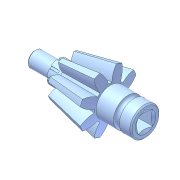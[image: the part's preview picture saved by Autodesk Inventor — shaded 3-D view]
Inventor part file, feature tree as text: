
AUTODESK INVENTOR PART (.ipt)
format: ipt  version: unknown  size: 373,248 bytes
history: native  units: in
note: dims shown in document units (in); Inventor stores cm internally (conversion verified against a paired STEP export)
features: sketch x10, extrude x6, plane x3, chamfer x3, revolve x2, other x1, loft x1, pattern_circular x1
ambient origin geometry x8: Origin, YZ Plane, XZ Plane, XY Plane, X Axis, Y Axis, Z Axis, Center Point
feature tree (27):
  revolve  "Revolution1"  [1 undecoded]
  other  "Work Point1"
  plane  "Work Plane7"
  sketch  "Sketch12"  dims[d10=90.0deg d88=0.1575in]
  extrude  "Extrusion8"  Depth=0.1575in
  extrude  "Extrusion9"  Depth=0.065in
  extrude  "Extrusion10"  Depth=0.0492in
  revolve  "Revolution3"  [1 undecoded]
  extrude  "Extrusion11"  Depth=0.315in
  chamfer  "Chamfer3"  Distance=0.2362in
  extrude  "Extrusion12"  Depth=0.1575in TaperAngle=0.0deg
  chamfer  "Chamfer4"  Angle=90.0deg  [1 undecoded]
  plane  "Work Plane9"
  loft  "Loft1"
  pattern_circular  "Circular Pattern3"  [2 undecoded]
  extrude  "Extrusion13"  Depth=0.0197in TaperAngle=30.0deg
  chamfer  "Chamfer5"  Distance=0.1181in
  sketch  "Sketch1"  dims[d1=0.1825in d2=0.0394in]
  sketch  "Sketch14"  dims[d89=0.0812in d90=0.065in]
  sketch  "Sketch15"  dims[d91=0.2756in d92=0.0492in]
  sketch  "Sketch16"  dims[d93=0.0984in d94=0.2756in]
  sketch  "Sketch17"  dims[d96=0.9449in d97=0.315in]
  sketch  "Sketch18"  dims[d98=0.9449in d99=0.2362in d100=0.0in]
  sketch  "Sketch19"  dims[d101=0.0787in d102=0.0in d103=0.1575in d104=0.0in]
  plane  "Work Plane8"
  sketch  "Sketch20"  dims[d105=0.0394in]
  sketch  "Sketch21"  dims[d106=0.0984in d107=90.0deg d108=0.0984in d109=0.1181in d110=0.0in d111=0.0197in d112=0.0787in d113=30.0deg d115=0.1181in d116=0.0in d117=0.0079in d118=0.0787in d119=30.0deg d120=0.0079in d121=0.0787in d122=30.0deg d123=0.0in d124=0.9579in d125=0.065in d126=0.9646in d127=0.0394in d128=0.0886in d129=0.0309in d131=0.0098in d132=0.0in d133=90.0deg d134=0.0in d135=90.0deg d136=3.1496in d137=360.0deg d139=0.0787in d140=0.1575in d141=0.0in d142=0.0984in d143=0.0in d144=0.0in]
note: 5 required parameter values undecoded (feature->parameter linkage not recoverable at this tier; creation-order binding heuristic only, values carry confidence <= 0.55)